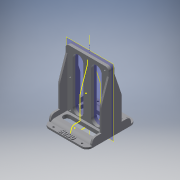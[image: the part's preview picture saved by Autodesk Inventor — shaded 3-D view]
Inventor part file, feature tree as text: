
AUTODESK INVENTOR PART (.ipt)
format: ipt  version: 2016 SP1 (Build 200210100, 210)  size: 644,608 bytes
history: native  units: in
note: dims shown in document units (in); Inventor stores cm internally (conversion verified against a paired STEP export)
features: projected_geometry x13, sketch x11, extrude x8, mirror x6, fillet x6, hole x3, plane x2, reference x2, other x1, pattern_circular x1
ambient origin geometry x8: Origin, YZ Plane, XZ Plane, XY Plane, X Axis, Y Axis, Z Axis, Center Point
bodies: Solid1 (feature_tree)
feature tree (53):
  sketch  "Sketch1"  dims[d0=0.25in d1=0.3in]
  extrude  "Extrusion1"  Depth=0.25in
  hole  "Hole1"  [1 undecoded]
  extrude  "Extrusion2"  Depth=0.375in
  extrude  "Extrusion3"  Depth=0.4in TaperAngle=0.0deg
  plane  "Work Plane1"
  mirror  "Mirror1"
  fillet  "Fillet1"  Radius=2.75in
  hole  "Hole3"  [1 undecoded]
  extrude  "Extrusion4"  Depth=0.125in
  fillet  "Fillet2"  Radius=0.125in
  fillet  "Fillet3"  Radius=2.0in
  plane  "Work Plane2"
  mirror  "Mirror2"
  mirror  "Mirror3"
  mirror  "Mirror4"
  mirror  "Mirror5"
  extrude  "Extrusion5"  Depth=0.25in
  fillet  "Fillet4"  Radius=0.375in
  hole  "Hole4"  [1 undecoded]
  mirror  "Mirror6"
  fillet  "Fillet5"  Radius=2.0in
  extrude  "Extrusion6"  Depth=0.375in
  sketch  "Sketch10"  dims[d43=1.0in d44=0.25in d45=0.375in]
  other  "Work Axis1"
  pattern_circular  "Circular Pattern1"  [2 undecoded]
  fillet  "Fillet6"  Radius=0.7874in
  extrude  "Extrusion7"  Depth=0.375in
  extrude  "Extrusion8"  Depth=1.0in
  sketch  "Sketch3"  dims[d2=0.3in d3=2.446in]
  projected_geometry  "Projected Loop3"
  sketch  "Sketch4"  dims[d4=1.646in d5=0.375in]
  projected_geometry  "Projected Loop4"
  sketch  "Sketch5"  dims[d6=0.25in d7=0.4in d8=0.0in]
  projected_geometry  "Projected Loop5"
  projected_geometry  "Projected Loop6"
  sketch  "Sketch6"  dims[d9=0.125in d10=0.75in d11=0.375in d12=0.25in d13=0.5635in d14=0.3875in d15=0.0in d23=2.75in]
  projected_geometry  "Projected Loop7"
  reference  "Reference1"
  sketch  "Sketch7"  dims[d24=0.25in d25=0.0in d28=0.125in d29=0.0in]
  reference  "Reference2"
  projected_geometry  "Projected Loop8"
  sketch  "Sketch8"  dims[d30=0.25in]
  projected_geometry  "Projected Loop9"
  sketch  "Sketch9"  dims[d31=0.125in d32=0.75in d33=0.375in d34=0.25in d35=0.5635in d36=0.3875in d37=0.0in d38=3.5in d39=0.125in d40=0.0in d41=2.0in]
  projected_geometry  "Projected Loop10"
  projected_geometry  "Projected Loop11"
  projected_geometry  "Projected Loop12"
  sketch  "Sketch11"  dims[d46=0.125in d47=0.0in d48=0.375in d50=2.0in]
  projected_geometry  "Projected Loop13"
  sketch  "Sketch12"  dims[d51=0.125in d52=0.75in d53=0.375in d54=0.25in d55=0.5635in d56=0.3875in d57=0.0in d58=0.375in d59=0.0625in d60=0.0in d61=0.7874in d62=360.0deg d64=0.375in d65=0.6561in d66=0.575in d67=0.75in d68=3.0in d69=1.125in d70=0.625in d71=1.0in d72=0.0in d73=2.0in d74=0.5in d75=0.475in d76=1.0in d77=0.0in]
  projected_geometry  "Projected Loop14"
  projected_geometry  "Projected Loop15"
note: 5 required parameter values undecoded (feature->parameter linkage not recoverable at this tier; creation-order binding heuristic only, values carry confidence <= 0.55)
